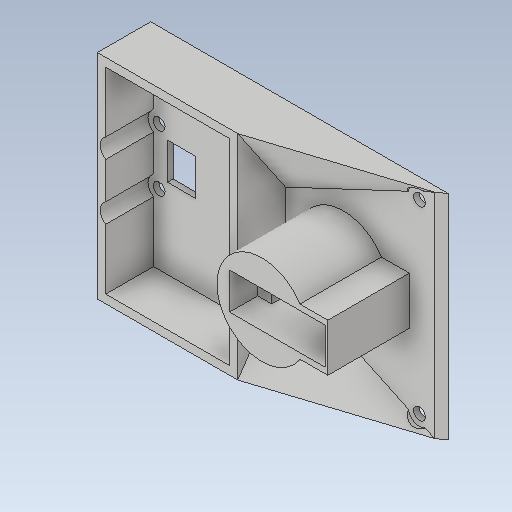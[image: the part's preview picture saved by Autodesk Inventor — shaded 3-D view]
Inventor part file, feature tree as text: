
AUTODESK INVENTOR PART (.ipt)
format: ipt  version: 2020 (Build 240168000, 168)  size: 293,888 bytes
history: native  units: mm
features: sketch x13, reference x13, extrude x10, other x6, loft x2, projected_geometry x2, plane x1, hole x1
ambient origin geometry x8: Origin, YZ Plane, XZ Plane, XY Plane, X Axis, Y Axis, Z Axis, Center Point
bodies: Solid1 (feature_tree)
feature tree (48):
  extrude  "Extrusion1"  Depth=76.0mm TaperAngle=0.0deg
  extrude  "Extrusion2"  Depth=3.0mm
  extrude  "Extrusion3"  Depth=3.0mm
  sketch  "3D Sketch1"
  sketch  "Sketch4"  dims[d8=3.0mm d9=17.0mm d10=0.0mm]
  loft  "Loft1"
  loft  "Loft2"
  extrude  "Extrusion5"  TaperAngle=0.0deg  [1 undecoded]
  extrude  "Extrusion6"  TaperAngle=0.0deg  [1 undecoded]
  sketch  "Sketch8"  dims[d17=0.0mm d18=90.0deg d19=0.0mm d20=90.0deg]
  plane  "Work Plane1"
  extrude  "Extrusion7"  Depth=13.0mm
  hole  "Hole1"  [1 undecoded]
  extrude  "Extrusion8"  Depth=6.0mm
  extrude  "Extrusion9"  Depth=2.0mm
  extrude  "Extrusion10"  Depth=19.0mm TaperAngle=0.0deg
  extrude  "Extrusion12"  Depth=0.5mm
  sketch  "Sketch1"  dims[d0=2.0mm d1=0.0mm d2=76.0mm d3=0.0mm]
  reference  "Reference1"
  sketch  "Sketch2"  dims[d4=50.0mm d5=3.0mm]
  reference  "Reference2"
  sketch  "Sketch3"  dims[d6=3.0mm d7=3.0mm]
  projected_geometry  "Projected Loop1"
  projected_geometry  "Projected Loop2"
  sketch  "Sketch6"  dims[d11=25.0mm d12=25.0mm]
  sketch  "Sketch7"  dims[d13=0.0mm d14=90.0deg d15=0.0mm d16=90.0deg]
  reference  "Reference11"
  reference  "Reference12"
  reference  "Reference13"
  reference  "Reference14"
  reference  "Reference15"
  sketch  "Sketch9"  dims[d25=24.0mm d26=13.0mm]
  reference  "Reference16"
  reference  "Reference17"
  sketch  "Sketch10"  dims[d27=15.0mm d29=19.0mm d30=0.0mm]
  sketch  "Sketch11"  dims[d31=6.0mm d32=6.0mm]
  reference  "Reference18"
  reference  "Reference19"
  reference  "Reference20"
  reference  "Reference21"
  sketch  "Sketch12"  dims[d33=2.0mm d34=2.0mm]
  sketch  "Sketch15"  dims[d35=32.0mm d36=19.0mm d37=0.0mm d38=0.5mm d39=0.5mm d40=4.75mm d41=0.0mm d42=1.0mm d43=6.0mm d44=4.0mm d45=2.0mm d46=90.0deg d47=5.0mm d48=20.594885mm d49=3.5mm d50=9.0mm d51=14.0mm d52=3.0mm d53=0.0mm d54=0.0mm d55=10.0mm d56=0.0mm d57=8.0mm d58=8.0mm d59=8.0mm d60=8.0mm d61=10.0mm d62=0.0mm d73=10.0mm d74=13.0mm d75=5.0mm d76=4.0mm d77=14.0mm d78=21.0mm d79=10.0mm d80=0.0mm]
  other  "<userpath>\Desktop\3d\scanning-robot\Assembly1.iam"
  other  "Assembly1.iam"
  other  "base:1"
  other  "Tower Pro MG90S Micro servo:3"
  other  "Вал последний с чем то:1"
  other  "Крышка корпуса:1"
note: 3 required parameter values undecoded (feature->parameter linkage not recoverable at this tier; creation-order binding heuristic only, values carry confidence <= 0.55)
